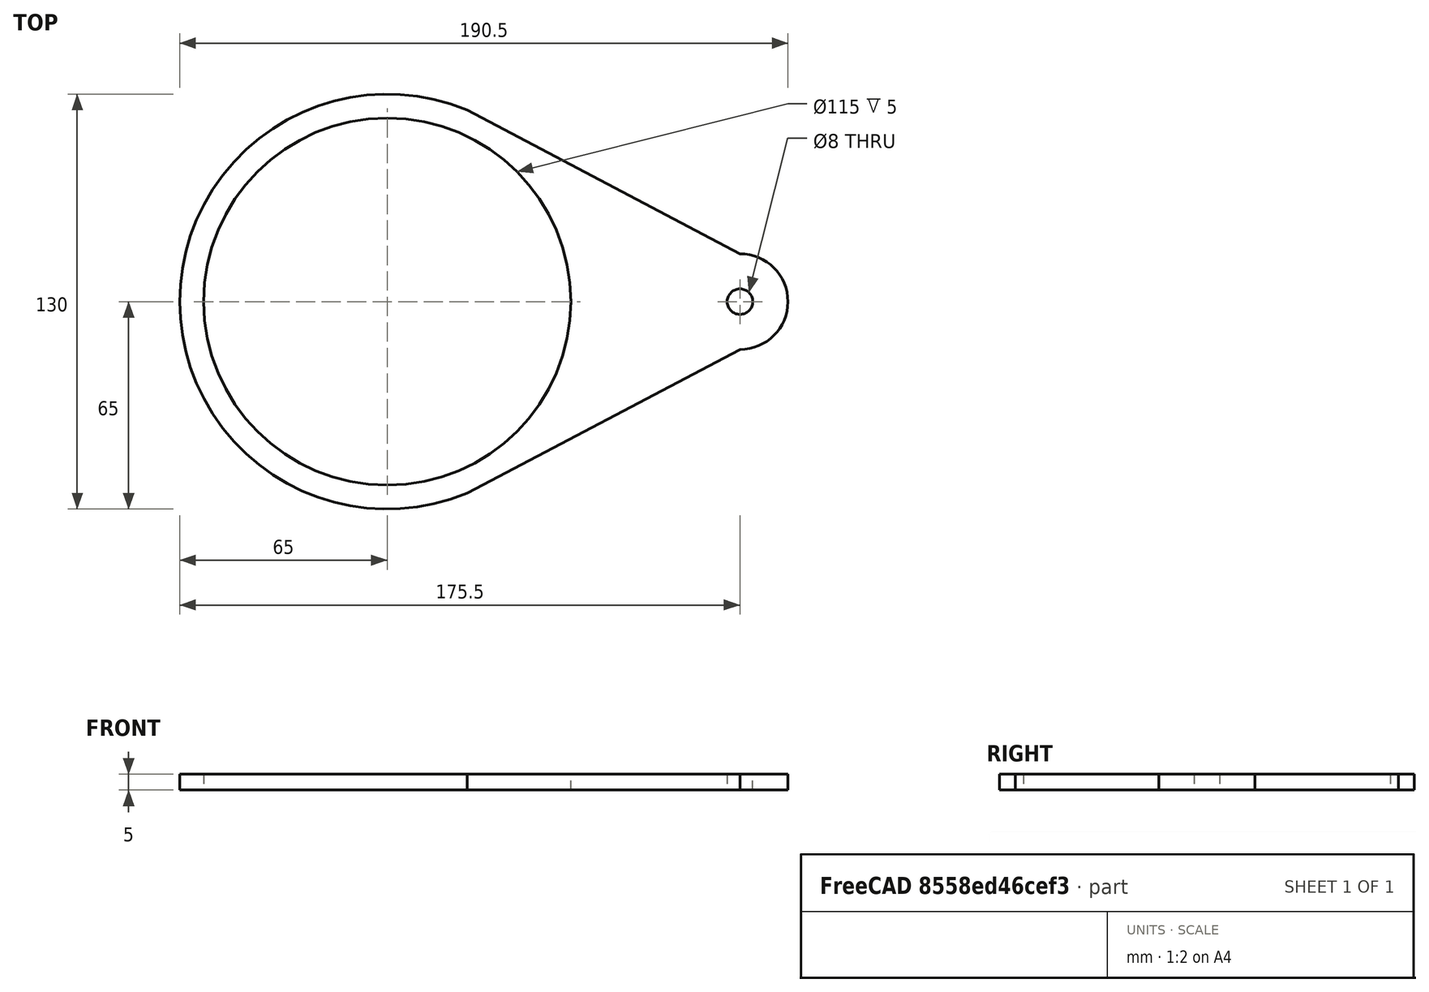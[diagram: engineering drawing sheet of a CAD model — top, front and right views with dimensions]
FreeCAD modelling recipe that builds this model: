
FCSTD DOCUMENT  (FreeCAD 1.0R39109 (Git))
Label: top
License: All rights reserved
LicenseURL: https://en.wikipedia.org/wiki/All_rights_reserved
objects: Sketcher::SketchObject×1, PartDesign::Pad×1, PartDesign::Body×1
note: 6 computed .brp shape members not serialized (recipe doc carries the construction recipe); baked Part::Feature solids carry a one-line shape summary decoded from their .brp

FEATURE [Sketcher::SketchObject] Sketch
  ArcFitTolerance = 1e-06
  AttachmentSupport = -> [XY_Plane]
  FullyConstrained = true
  MakeInternals = false
  MapMode = 5
  sketch-geometry (7):
    g0: Circle CenterX=0 CenterY=0 CenterZ=0 NormalX=0 NormalY=0 NormalZ=1 AngleXU=0 Radius=57.5
    g1: ArcOfCircle CenterX=0 CenterY=0 CenterZ=0 NormalX=0 NormalY=0 NormalZ=1 AngleXU=0 Radius=65 StartAngle=1.17601 EndAngle=5.10718
    g2: LineSegment StartX=25 StartY=60 StartZ=0 EndX=110.5 EndY=15 EndZ=0
    g3: LineSegment StartX=25 StartY=-60 StartZ=0 EndX=110.5 EndY=-15 EndZ=0
    g4: LineSegment [constr] StartX=57.5 StartY=0 StartZ=0 EndX=125.5 EndY=0 EndZ=0
    g5: ArcOfCircle CenterX=110.5 CenterY=0 CenterZ=0 NormalX=0 NormalY=0 NormalZ=1 AngleXU=0 Radius=15 StartAngle=4.71239 EndAngle=7.85398
    g6: Circle CenterX=110.5 CenterY=0 CenterZ=0 NormalX=0 NormalY=0 NormalZ=1 AngleXU=0 Radius=4
  constraints (21):
    c: Diameter(g0) = 115
    c: Coincident(g0,g-1)
    c: Coincident(g1,g0)
    c: Vertical(g1,g1)
    c: Diameter(g1) = 130
    c: Coincident(g2,g1)
    c: Coincident(g3,g1)
    c: Distance(g4) = 68
    c: Horizontal(g4)
    c: PointOnObject(g4,g0)
    c: Radius(g5) = 15
    c: Angle(g5) = 3.14159
    c: PointOnObject(g5,g4)
    c: Coincident(g3,g5)
    c: Vertical(g5,g3)
    c: PointOnObject(g4,g5)
    c: Horizontal(g5,g0)
    c: Coincident(g2,g5)
    c: DistanceX(g0,g1) = 25
    c: Diameter(g6) = 8
    c: Coincident(g6,g5)
FEATURE [PartDesign::Pad] Pad
  Direction = (0,0,1)
  Length = 5
  Length2 = 10
  Profile = -> Sketch
  ReferenceAxis = -> Sketch [N_Axis]
  Refine = true
  Suppressed = false
  Type = 0
FEATURE [PartDesign::Body] Body
  AllowCompound = false
  Group = -> [Sketch,Pad]
  Origin = -> Origin
  Tip = -> Pad
